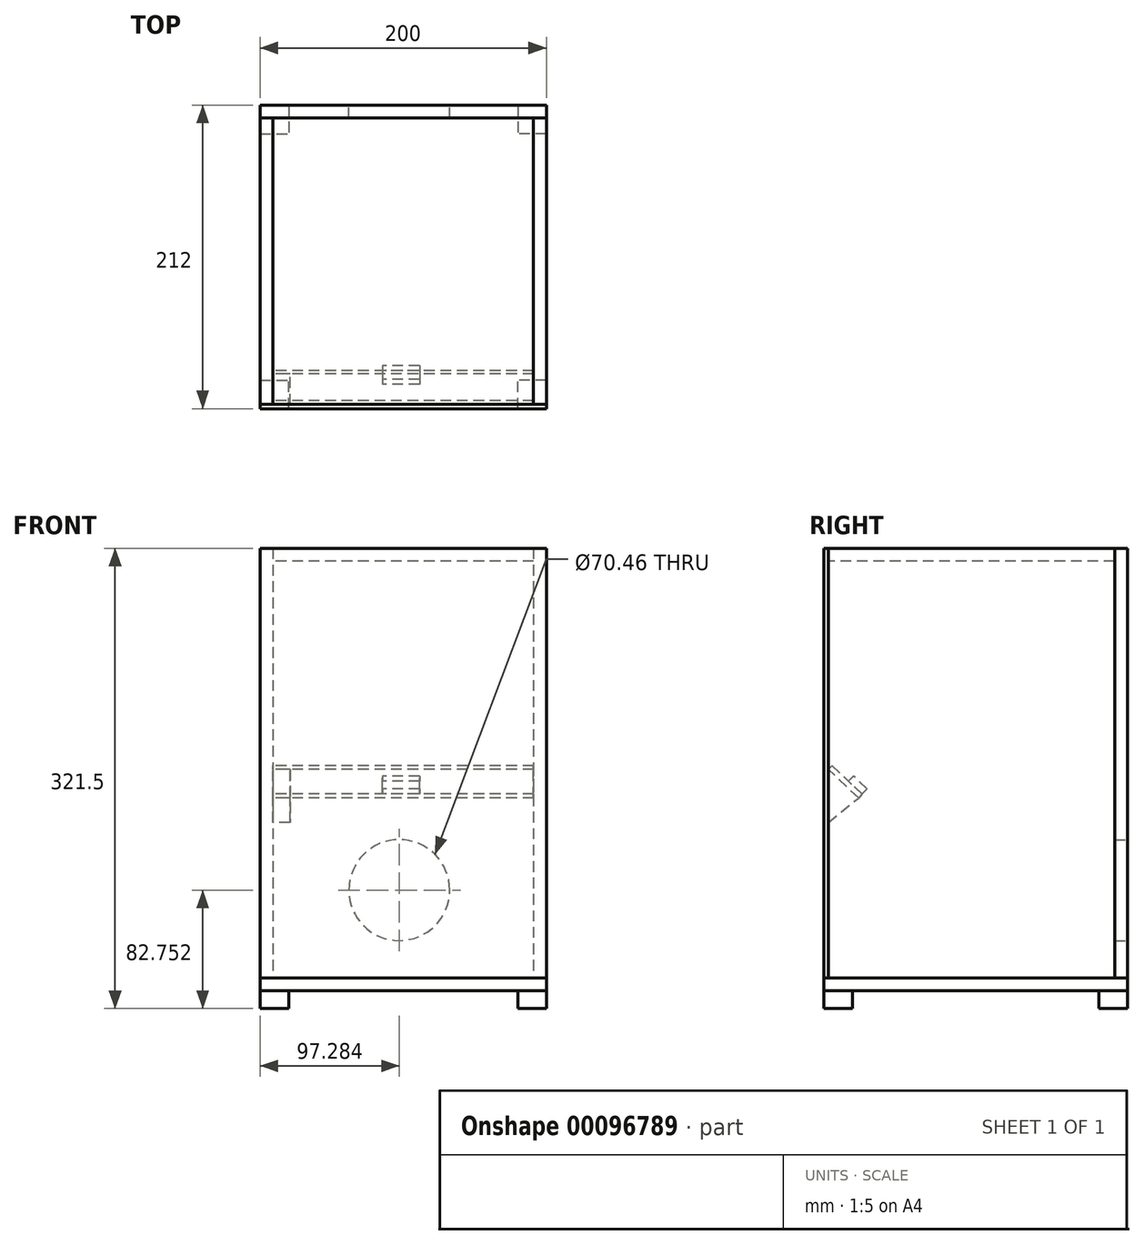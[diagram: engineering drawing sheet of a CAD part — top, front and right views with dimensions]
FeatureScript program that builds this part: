
annotation { "Feature Type Name" : "Feature", "Feature Type Description" : "" }
export const myFeature = defineFeature(function(context is Context, id is Id, definition is map)
    precondition{}
    {
        {
            var Q0;
            Q0=qCreatedBy(makeId("Front.planeOp"),FACE);
            var sketch = newSketch(context, id + "F0", { "sketchPlane" : qUnion([Q0])});
            skLineSegment(sketch, "E0.bottom", {"start": v(0, 0) * mm, "end": v(200, 0) * mm});
            skLineSegment(sketch, "E0.top", {"start": v(0, 300) * mm, "end": v(200, 300) * mm});
            skLineSegment(sketch, "E0.left", {"start": v(0, 0) * mm, "end": v(0, 300) * mm});
            skLineSegment(sketch, "E0.right", {"start": v(200, 0) * mm, "end": v(200, 300) * mm});
            skSolve(sketch);
        }
        {
            var Q0;
            Q0 = qSketchRegion(id + "F0", true);
            extrude(context, id + "F1", {"entities" : qUnion([Q0]), "depth" : 1.5 * mm});
        }
        {
            var Q0;
            Q0=makeQuery(id+"F1.opExtrude","CAP_FACE",FACE,{"disambiguationData":[OSD([sQuery(id+"F0.wireOp",EDGE,"E0.bottom"),sQuery(id+"F0.wireOp",EDGE,"E0.top"),sQuery(id+"F0.wireOp",EDGE,"E0.left"),sQuery(id+"F0.wireOp",EDGE,"E0.right")])],"isStart":false});
            extrude(context, id + "F2", {"entities" : qUnion([Q0]), "operationType" : NewBodyOperationType.ADD, "depth" : 1.5 * mm});
        }
        {
            var Q0;
            Q0=makeQuery(id+"F1.opExtrude","CAP_FACE",FACE,{"disambiguationData":[OSD([sQuery(id+"F0.wireOp",EDGE,"E0.bottom"),sQuery(id+"F0.wireOp",EDGE,"E0.top"),sQuery(id+"F0.wireOp",EDGE,"E0.left"),sQuery(id+"F0.wireOp",EDGE,"E0.right")])],"isStart":true});
            var sketch = newSketch(context, id + "F3", { "sketchPlane" : qUnion([Q0])});
            skLineSegment(sketch, "E1.bottom", {"start": v(0, 300) * mm, "end": v(-9, 300) * mm});
            skLineSegment(sketch, "E1.top", {"start": v(0, 0) * mm, "end": v(-9, 0) * mm});
            skLineSegment(sketch, "E1.left", {"start": v(0, 300) * mm, "end": v(0, 0) * mm});
            skLineSegment(sketch, "E1.right", {"start": v(-9, 300) * mm, "end": v(-9, 0) * mm});
            skSolve(sketch);
        }
        {
            var Q0;
            Q0 = qSketchRegion(id + "F3", true);
            extrude(context, id + "F4", {"entities" : qUnion([Q0]), "depth" : 200 * mm});
        }
        {
            var Q0;
            Q0=makeQuery(id+"F4.opExtrude","SWEPT_FACE",FACE,{"disambiguationData":[OSD([sQuery(id+"F3.wireOp",EDGE,"E1.right")])]});
            var sketch = newSketch(context, id + "F5", { "sketchPlane" : qUnion([Q0])});
            skLineSegment(sketch, "E2", {"start": v(0, 145.66) * mm, "end": v(0, 108.56) * mm});
            skLineSegment(sketch, "E3", {"start": v(0, 108.56) * mm, "end": v(21.22, 125.72) * mm});
            skLineSegment(sketch, "E4", {"start": v(21.22, 125.72) * mm, "end": v(0, 145.66) * mm});
            skSolve(sketch);
        }
        {
            var Q0;
            Q0 = qSketchRegion(id + "F5", true);
            extrude(context, id + "F6", {"entities" : qUnion([Q0]), "depth" : 12 * mm});
        }
        {
            var Q0;
            Q0=makeQuery(id+"F4.opExtrude","SWEPT_FACE",FACE,{"disambiguationData":[OSD([sQuery(id+"F3.wireOp",EDGE,"E1.right")])]});
            var sketch = newSketch(context, id + "F7", { "sketchPlane" : qUnion([Q0])});
            skLineSegment(sketch, "E5", {"start": v(21.22, 125.72) * mm, "end": v(0, 145.66) * mm});
            skLineSegment(sketch, "E6", {"start": v(0, 145.66) * mm, "end": v(2.48, 148.3) * mm});
            skLineSegment(sketch, "E7", {"start": v(2.48, 148.3) * mm, "end": v(23.7, 128.36) * mm});
            skLineSegment(sketch, "E8", {"start": v(23.7, 128.36) * mm, "end": v(21.22, 125.72) * mm});
            skSolve(sketch);
        }
        {
            var Q0;
            Q0 = qSketchRegion(id + "F7", true);
            extrude(context, id + "F8", {"entities" : qUnion([Q0]), "depth" : 182 * mm});
        }
        {
            var Q0;
            Q0=makeQuery(id+"F8.opExtrude","SWEPT_FACE",FACE,{"disambiguationData":[OSD([sQuery(id+"F7.wireOp",EDGE,"E7")])]});
            var sketch = newSketch(context, id + "F9", { "sketchPlane" : qUnion([Q0])});
            skLineSegment(sketch, "E9.bottom", {"start": v(111.45, -70.62) * mm, "end": v(85.4, -70.62) * mm});
            skLineSegment(sketch, "E9.top", {"start": v(111.45, -83.76) * mm, "end": v(85.4, -83.76) * mm});
            skLineSegment(sketch, "E9.left", {"start": v(111.45, -70.62) * mm, "end": v(111.45, -83.76) * mm});
            skLineSegment(sketch, "E9.right", {"start": v(85.4, -70.62) * mm, "end": v(85.4, -83.76) * mm});
            skSolve(sketch);
        }
        {
            var Q0;
            Q0 = qSketchRegion(id + "F9", true);
            extrude(context, id + "F10", {"entities" : qUnion([Q0]), "depth" : 5 * mm});
        }
        {
            var Q0;
            Q0=makeQuery(id+"F4.opExtrude","SWEPT_FACE",FACE,{"disambiguationData":[OSD([sQuery(id+"F3.wireOp",EDGE,"E1.right")])]});
            var sketch = newSketch(context, id + "F11", { "sketchPlane" : qUnion([Q0])});
            skLineSegment(sketch, "E10.bottom", {"start": v(200, 300) * mm, "end": v(0, 300) * mm});
            skLineSegment(sketch, "E10.top", {"start": v(200, 291) * mm, "end": v(0, 291) * mm});
            skLineSegment(sketch, "E10.left", {"start": v(200, 300) * mm, "end": v(200, 291) * mm});
            skLineSegment(sketch, "E10.right", {"start": v(0, 300) * mm, "end": v(0, 291) * mm});
            skSolve(sketch);
        }
        {
            var Q0;
            Q0 = qSketchRegion(id + "F11", true);
            extrude(context, id + "F12", {"entities" : qUnion([Q0]), "depth" : 182 * mm});
        }
        {
            var Q0;
            Q0=makeQuery(id+"F12.opExtrude","CAP_FACE",FACE,{"disambiguationData":[OSD([sQuery(id+"F11.wireOp",EDGE,"E10.bottom"),sQuery(id+"F11.wireOp",EDGE,"E10.top"),sQuery(id+"F11.wireOp",EDGE,"E10.left"),sQuery(id+"F11.wireOp",EDGE,"E10.right")])],"isStart":false});
            var sketch = newSketch(context, id + "F13", { "sketchPlane" : qUnion([Q0])});
            skLineSegment(sketch, "E11.bottom", {"start": v(200, 300) * mm, "end": v(0, 300) * mm});
            skLineSegment(sketch, "E11.top", {"start": v(200, 0) * mm, "end": v(0, 0) * mm});
            skLineSegment(sketch, "E11.left", {"start": v(200, 300) * mm, "end": v(200, 0) * mm});
            skLineSegment(sketch, "E11.right", {"start": v(0, 300) * mm, "end": v(0, 0) * mm});
            skSolve(sketch);
        }
        {
            var Q0;
            Q0 = qSketchRegion(id + "F13", true);
            extrude(context, id + "F14", {"entities" : qUnion([Q0]), "depth" : 9 * mm});
        }
        {
            var Q0;
            Q0=makeQuery(id+"F14.opExtrude","SWEPT_FACE",FACE,{"disambiguationData":[OSD([sQuery(id+"F13.wireOp",EDGE,"E11.left")])]});
            var sketch = newSketch(context, id + "F15", { "sketchPlane" : qUnion([Q0])});
            skLineSegment(sketch, "E12.bottom", {"start": v(-200, 300) * mm, "end": v(0, 300) * mm});
            skLineSegment(sketch, "E12.top", {"start": v(-200, 0) * mm, "end": v(0, 0) * mm});
            skLineSegment(sketch, "E12.left", {"start": v(-200, 300) * mm, "end": v(-200, 0) * mm});
            skLineSegment(sketch, "E12.right", {"start": v(0, 300) * mm, "end": v(0, 0) * mm});
            skSolve(sketch);
        }
        {
            var Q0;
            Q0 = qSketchRegion(id + "F15", true);
            extrude(context, id + "F16", {"entities" : qUnion([Q0]), "depth" : 9 * mm});
        }
        {
            var Q0;
            Q0=makeQuery(id+"F16.opExtrude","CAP_FACE",FACE,{"disambiguationData":[OSD([sQuery(id+"F15.wireOp",EDGE,"E12.bottom"),sQuery(id+"F15.wireOp",EDGE,"E12.top"),sQuery(id+"F15.wireOp",EDGE,"E12.left"),sQuery(id+"F15.wireOp",EDGE,"E12.right")])],"isStart":false});
            var sketch = newSketch(context, id + "F17", { "sketchPlane" : qUnion([Q0])});
            skCircle(sketch, "E13", {"center": v(-97.28, 61.25) * mm, "radius": 35.23 * mm});
            skSolve(sketch);
        }
        {
            var Q0;
            Q0 = qSketchRegion(id + "F17", true);
            extrude(context, id + "F18", {"entities" : qUnion([Q0]), "operationType" : NewBodyOperationType.REMOVE, "oppositeDirection" : true, "depth" : 9 * mm});
        }
        {
            var Q0;
            {var subQ0=sQuery(id+"F0.wireOp",EDGE,"E0.bottom");Q0=makeQuery(id+"F2.boolean.opBoolean","MERGE",FACE,{"derivedFrom":[makeQuery(id+"F1.opExtrude","SWEPT_FACE",FACE,{"disambiguationData":[OSD([subQ0])]}),makeQuery(id+"F2.opExtrude","SWEPT_FACE",FACE,{"disambiguationData":[OSD([subQ0])]})]});}
            var sketch = newSketch(context, id + "F19", { "sketchPlane" : qUnion([Q0])});
            skLineSegment(sketch, "E14.bottom", {"start": v(0, 3) * mm, "end": v(200, 3) * mm});
            skLineSegment(sketch, "E14.top", {"start": v(0, -209) * mm, "end": v(200, -209) * mm});
            skLineSegment(sketch, "E14.left", {"start": v(0, 3) * mm, "end": v(0, -209) * mm});
            skLineSegment(sketch, "E14.right", {"start": v(200, 3) * mm, "end": v(200, -209) * mm});
            skSolve(sketch);
        }
        {
            var Q0;
            Q0 = qSketchRegion(id + "F19", true);
            extrude(context, id + "F20", {"entities" : qUnion([Q0]), "depth" : 9 * mm});
        }
        {
            var Q0;
            Q0=makeQuery(id+"F20.opExtrude","CAP_FACE",FACE,{"disambiguationData":[OSD([sQuery(id+"F19.wireOp",EDGE,"E14.bottom"),sQuery(id+"F19.wireOp",EDGE,"E14.top"),sQuery(id+"F19.wireOp",EDGE,"E14.left"),sQuery(id+"F19.wireOp",EDGE,"E14.right")])],"isStart":false});
            var sketch = newSketch(context, id + "F21", { "sketchPlane" : qUnion([Q0])});
            skLineSegment(sketch, "E15.bottom", {"start": v(0, 3) * mm, "end": v(20, 3) * mm});
            skLineSegment(sketch, "E15.top", {"start": v(0, -17) * mm, "end": v(20, -17) * mm});
            skLineSegment(sketch, "E15.left", {"start": v(0, 3) * mm, "end": v(0, -17) * mm});
            skLineSegment(sketch, "E15.right", {"start": v(20, 3) * mm, "end": v(20, -17) * mm});
            skSolve(sketch);
        }
        {
            var Q0;
            Q0=makeQuery(id+"F21.imprint","IMPRINT",FACE,{"disambiguationData":[TD([[makeQuery(id+"F21.imprint","IMPRINT",EDGE,{"derivedFrom":sQuery(id+"F21.wireOp",EDGE,"E15.bottom")}),-1.0]])]});
            extrude(context, id + "F22", {"entities" : qUnion([Q0]), "depth" : 12.5 * mm});
        }
        {
            var Q0;
            Q0=makeQuery(id+"F20.opExtrude","CAP_FACE",FACE,{"disambiguationData":[OSD([sQuery(id+"F19.wireOp",EDGE,"E14.bottom"),sQuery(id+"F19.wireOp",EDGE,"E14.top"),sQuery(id+"F19.wireOp",EDGE,"E14.left"),sQuery(id+"F19.wireOp",EDGE,"E14.right")])],"isStart":false});
            var sketch = newSketch(context, id + "F23", { "sketchPlane" : qUnion([Q0])});
            skLineSegment(sketch, "E16.bottom", {"start": v(200, 3) * mm, "end": v(180, 3) * mm});
            skLineSegment(sketch, "E16.top", {"start": v(200, -17) * mm, "end": v(180, -17) * mm});
            skLineSegment(sketch, "E16.left", {"start": v(200, 3) * mm, "end": v(200, -17) * mm});
            skLineSegment(sketch, "E16.right", {"start": v(180, 3) * mm, "end": v(180, -17) * mm});
            skSolve(sketch);
        }
        {
            var Q0;
            Q0=makeQuery(id+"F23.imprint","IMPRINT",FACE,{"disambiguationData":[TD([[makeQuery(id+"F23.imprint","IMPRINT",EDGE,{"derivedFrom":sQuery(id+"F23.wireOp",EDGE,"E16.bottom")}),-1.0]])]});
            extrude(context, id + "F24", {"entities" : qUnion([Q0]), "depth" : 12.5 * mm});
        }
        {
            var Q0;
            Q0=makeQuery(id+"F20.opExtrude","CAP_FACE",FACE,{"disambiguationData":[OSD([sQuery(id+"F19.wireOp",EDGE,"E14.bottom"),sQuery(id+"F19.wireOp",EDGE,"E14.top"),sQuery(id+"F19.wireOp",EDGE,"E14.left"),sQuery(id+"F19.wireOp",EDGE,"E14.right")])],"isStart":false});
            var sketch = newSketch(context, id + "F25", { "sketchPlane" : qUnion([Q0])});
            skLineSegment(sketch, "E17.bottom", {"start": v(200, -209) * mm, "end": v(180, -209) * mm});
            skLineSegment(sketch, "E17.top", {"start": v(200, -189) * mm, "end": v(180, -189) * mm});
            skLineSegment(sketch, "E17.left", {"start": v(200, -209) * mm, "end": v(200, -189) * mm});
            skLineSegment(sketch, "E17.right", {"start": v(180, -209) * mm, "end": v(180, -189) * mm});
            skSolve(sketch);
        }
        {
            var Q0;
            Q0=makeQuery(id+"F25.imprint","IMPRINT",FACE,{"disambiguationData":[TD([[makeQuery(id+"F25.imprint","IMPRINT",EDGE,{"derivedFrom":sQuery(id+"F25.wireOp",EDGE,"E17.bottom")}),1.0]])]});
            extrude(context, id + "F26", {"entities" : qUnion([Q0]), "depth" : 12.5 * mm});
        }
        {
            var Q0;
            Q0=makeQuery(id+"F20.opExtrude","CAP_FACE",FACE,{"disambiguationData":[OSD([sQuery(id+"F19.wireOp",EDGE,"E14.bottom"),sQuery(id+"F19.wireOp",EDGE,"E14.top"),sQuery(id+"F19.wireOp",EDGE,"E14.left"),sQuery(id+"F19.wireOp",EDGE,"E14.right")])],"isStart":false});
            var sketch = newSketch(context, id + "F27", { "sketchPlane" : qUnion([Q0])});
            skLineSegment(sketch, "E18.bottom", {"start": v(0, -209) * mm, "end": v(20, -209) * mm});
            skLineSegment(sketch, "E18.top", {"start": v(0, -189) * mm, "end": v(20, -189) * mm});
            skLineSegment(sketch, "E18.left", {"start": v(0, -209) * mm, "end": v(0, -189) * mm});
            skLineSegment(sketch, "E18.right", {"start": v(20, -209) * mm, "end": v(20, -189) * mm});
            skSolve(sketch);
        }
        {
            var Q0;
            Q0=makeQuery(id+"F27.imprint","IMPRINT",FACE,{"disambiguationData":[TD([[makeQuery(id+"F27.imprint","IMPRINT",EDGE,{"derivedFrom":sQuery(id+"F27.wireOp",EDGE,"E18.bottom")}),1.0]])]});
            extrude(context, id + "F28", {"entities" : qUnion([Q0]), "depth" : 12.5 * mm});
        }
    });
